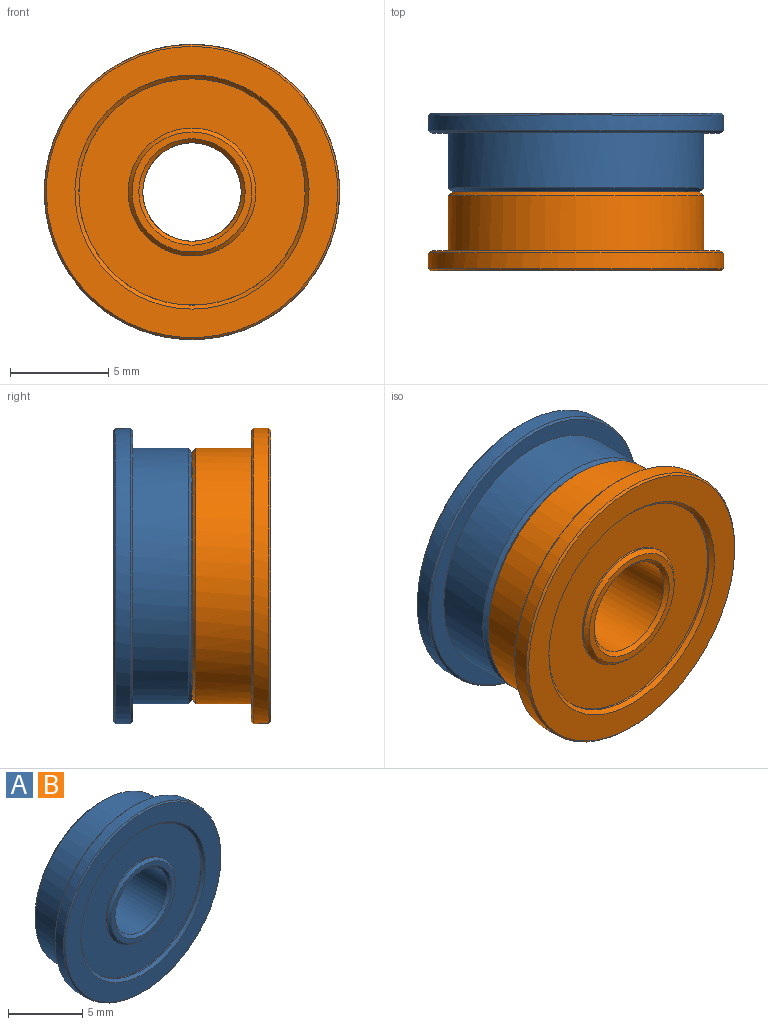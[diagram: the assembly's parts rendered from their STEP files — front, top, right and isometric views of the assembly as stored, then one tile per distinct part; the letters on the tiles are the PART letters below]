
ASSEMBLY  parts=2 mates=1
PART A: 23 faces, bbox 15x4x15 mm
  f0: cylinder r=6.5mm len=13mm, axis (0,1,0), area 114.4mm2, adj f1,f16
  f1: cone r=6.5mm half-angle=45deg, axis (0,-1,0), area 11.4mm2, adj f0,f17
  f2: cone r=7.5mm half-angle=45deg, axis (0,-1,0), area 6.6mm2, adj f4,f16
  f3: cone r=5.95mm half-angle=45deg, axis (0,1,0), area 10.4mm2, adj f5,f17
  f4: cylinder r=7.5mm len=15mm, axis (0,1,0), area 37.7mm2, adj f2,f6
  f5: cylinder r=5.75mm len=11.5mm, axis (0,-1,0), area 3.6mm2, adj f3,f18
  f6: cone r=7.5mm half-angle=45deg, axis (0,1,0), area 6.6mm2, adj f4,f19
  f7: cylinder r=3.25mm len=6.5mm, axis (0,-1,0), area 2mm2, adj f9,f18
  f8: cone r=5.95mm half-angle=45deg, axis (0,-1,0), area 10.4mm2, adj f10,f19
  f9: cone r=3.25mm half-angle=45deg, axis (0,-1,0), area 5.6mm2, adj f7,f20
  f10: cylinder r=5.75mm len=11.5mm, axis (0,1,0), area 3.6mm2, adj f8,f21
  f11: cone r=2.7mm half-angle=45deg, axis (0,1,0), area 4.6mm2, adj f13,f20
  f12: cylinder r=3.25mm len=6.5mm, axis (0,1,0), area 2mm2, adj f14,f21
  f13: cylinder r=2.5mm len=5mm, axis (0,-1,0), area 56.5mm2, adj f11,f15
  f14: cone r=3.25mm half-angle=45deg, axis (0,1,0), area 5.6mm2, adj f12,f22
  f15: cone r=2.7mm half-angle=45deg, axis (0,-1,0), area 4.6mm2, adj f13,f22
  f16: plane 14.8x14.8mm, normal (0,1,0), area 39.3mm2, adj f0,f2
  f17: plane 12.6x12.6mm, normal (0,1,0), area 13.5mm2, adj f1,f3
  f18: plane 11.5x11.5mm, normal (0,1,0), area 70.7mm2, adj f5,f7
  f19: plane 14.8x14.8mm, normal (0,-1,0), area 60.8mm2, adj f6,f8
  f20: plane 6.1x6.1mm, normal (0,1,0), area 6.3mm2, adj f9,f11
  f21: plane 11.5x11.5mm, normal (0,-1,0), area 70.7mm2, adj f10,f12
  f22: plane 6.1x6.1mm, normal (0,-1,0), area 6.3mm2, adj f14,f15
PART B: same geometry as A
PLACE A rot(axis=(1,0,0),180deg) t=(120.16,-9.85,-452.26)mm
PLACE B t=(120.16,-37.85,427.64)mm
MATE fastened A.f4 <-> B.f4  axis (0,-1,0) through (110.84,-23.85,-12.31)mm
